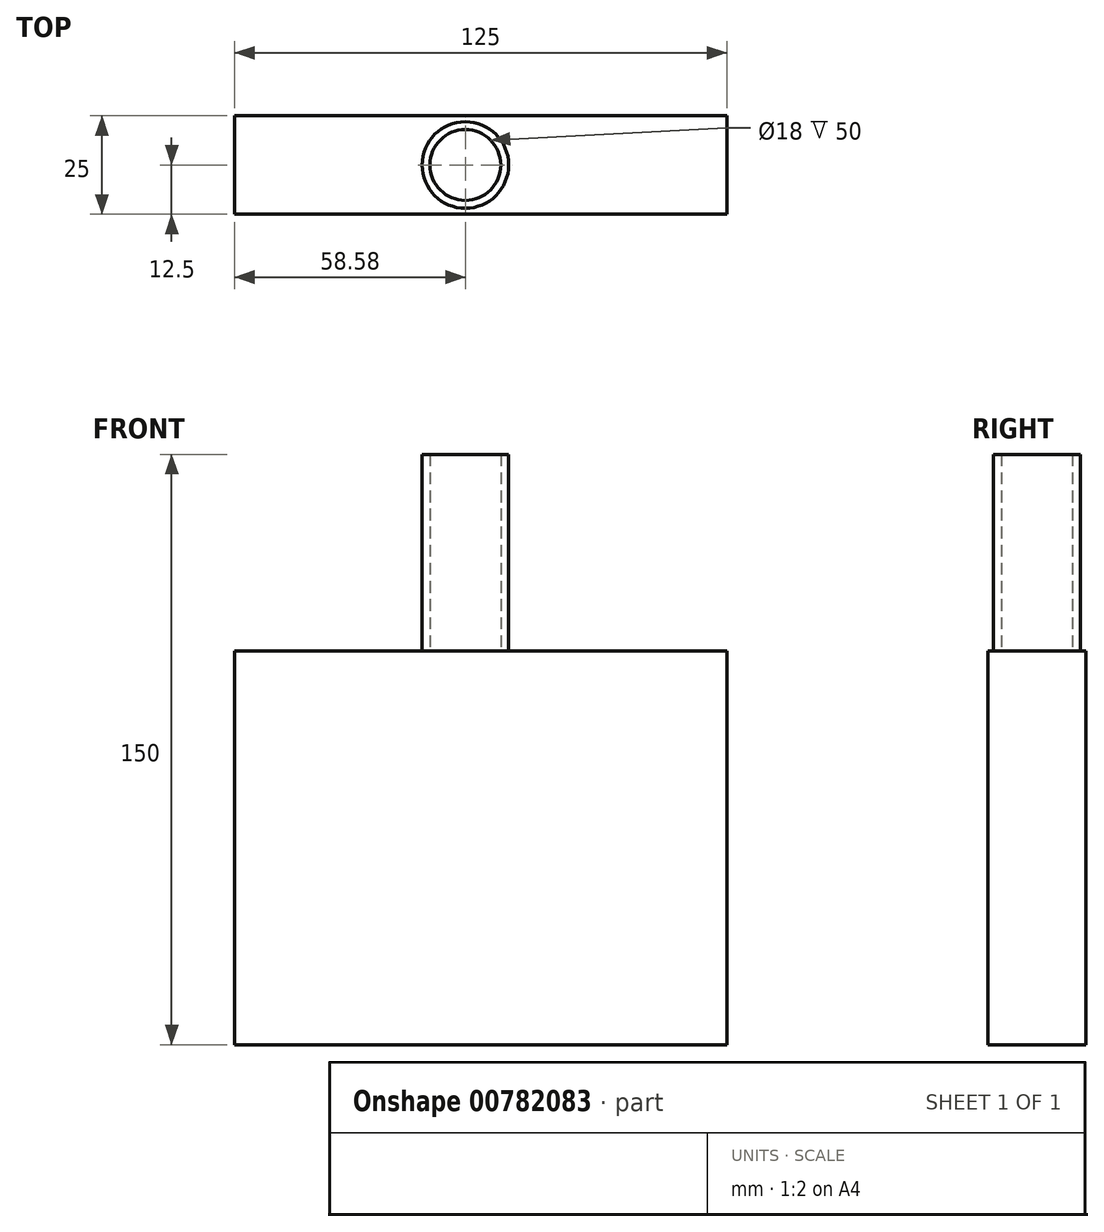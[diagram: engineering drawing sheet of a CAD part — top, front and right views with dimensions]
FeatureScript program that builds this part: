
annotation { "Feature Type Name" : "Feature", "Feature Type Description" : "" }
export const myFeature = defineFeature(function(context is Context, id is Id, definition is map)
    precondition{}
    {
        {
            var Q0;
            Q0=qCreatedBy(makeId("Top.planeOp"),FACE);
            var sketch = newSketch(context, id + "F0", { "sketchPlane" : qUnion([Q0])});
            skLineSegment(sketch, "E0.bottom", {"start": v(62.5, 12.5) * mm, "end": v(-62.5, 12.5) * mm});
            skLineSegment(sketch, "E0.top", {"start": v(62.5, -12.5) * mm, "end": v(-62.5, -12.5) * mm});
            skLineSegment(sketch, "E0.left", {"start": v(62.5, 12.5) * mm, "end": v(62.5, -12.5) * mm});
            skLineSegment(sketch, "E0.right", {"start": v(-62.5, 12.5) * mm, "end": v(-62.5, -12.5) * mm});
            skPoint(sketch, "E0.middle", {"position": v(0, 0) * mm});
            skSolve(sketch);
        }
        {
            var Q0;
            Q0=makeQuery(id+"F0.imprint","IMPRINT",FACE,{"disambiguationData":[TD([[makeQuery(id+"F0.imprint","IMPRINT",EDGE,{"derivedFrom":sQuery(id+"F0.wireOp",EDGE,"E0.bottom")}),1.0]])]});
            extrude(context, id + "F1", {"entities" : qUnion([Q0]), "depth" : 100 * mm, "offsetDistance" : 25.4 * mm});
        }
        {
            var Q0;
            Q0=makeQuery(id+"F1.opExtrude","CAP_FACE",FACE,{"disambiguationData":[OSD([sQuery(id+"F0.wireOp",EDGE,"E0.bottom"),sQuery(id+"F0.wireOp",EDGE,"E0.top"),sQuery(id+"F0.wireOp",EDGE,"E0.left"),sQuery(id+"F0.wireOp",EDGE,"E0.right")])],"isStart":false});
            var sketch = newSketch(context, id + "F2", { "sketchPlane" : qUnion([Q0])});
            skLineSegment(sketch, "E1", {"start": v(-3.92, 12.5) * mm, "end": v(-3.92, -12.5) * mm});
            skPoint(sketch, "E1.endSnap0", {"position": v(0, -12.5) * mm});
            skCircle(sketch, "E2", {"center": v(-3.92, 0) * mm, "radius": 11 * mm});
            skCircle(sketch, "E3.0", {"center": v(-3.92, 0) * mm, "radius": 9 * mm});
            skSolve(sketch);
        }
        {
            var Q0;
            {var subQ0=sQuery(id+"F2.wireOp",EDGE,"E2");var subQ1=sQuery(id+"F2.wireOp",EDGE,"E1");var subQ2=makeQuery(id+"F2.imprint","INTERSECT",VERTEX,{"disambiguationData":[OD(0.0)],"derivedFrom":[subQ1,subQ0]});Q0=makeQuery(id+"F2.imprint","IMPRINT",FACE,{"disambiguationData":[TD([[makeQuery(id+"F2.imprint","IMPRINT",EDGE,{"disambiguationData":[TD([[subQ2,-1.0]])],"derivedFrom":subQ1}),-1.0]])]});}
            var Q1;
            {var subQ0=sQuery(id+"F2.wireOp",EDGE,"E2");var subQ1=sQuery(id+"F2.wireOp",EDGE,"E1");var subQ2=makeQuery(id+"F2.imprint","INTERSECT",VERTEX,{"disambiguationData":[OD(0.0)],"derivedFrom":[subQ1,subQ0]});Q1=makeQuery(id+"F2.imprint","IMPRINT",FACE,{"disambiguationData":[TD([[makeQuery(id+"F2.imprint","IMPRINT",EDGE,{"disambiguationData":[TD([[subQ2,-1.0]])],"derivedFrom":subQ1}),1.0]])]});}
            extrude(context, id + "F3", {"entities" : qUnion([Q0, Q1]), "operationType" : NewBodyOperationType.ADD, "depth" : 50 * mm, "offsetDistance" : 25.4 * mm});
        }
    });
